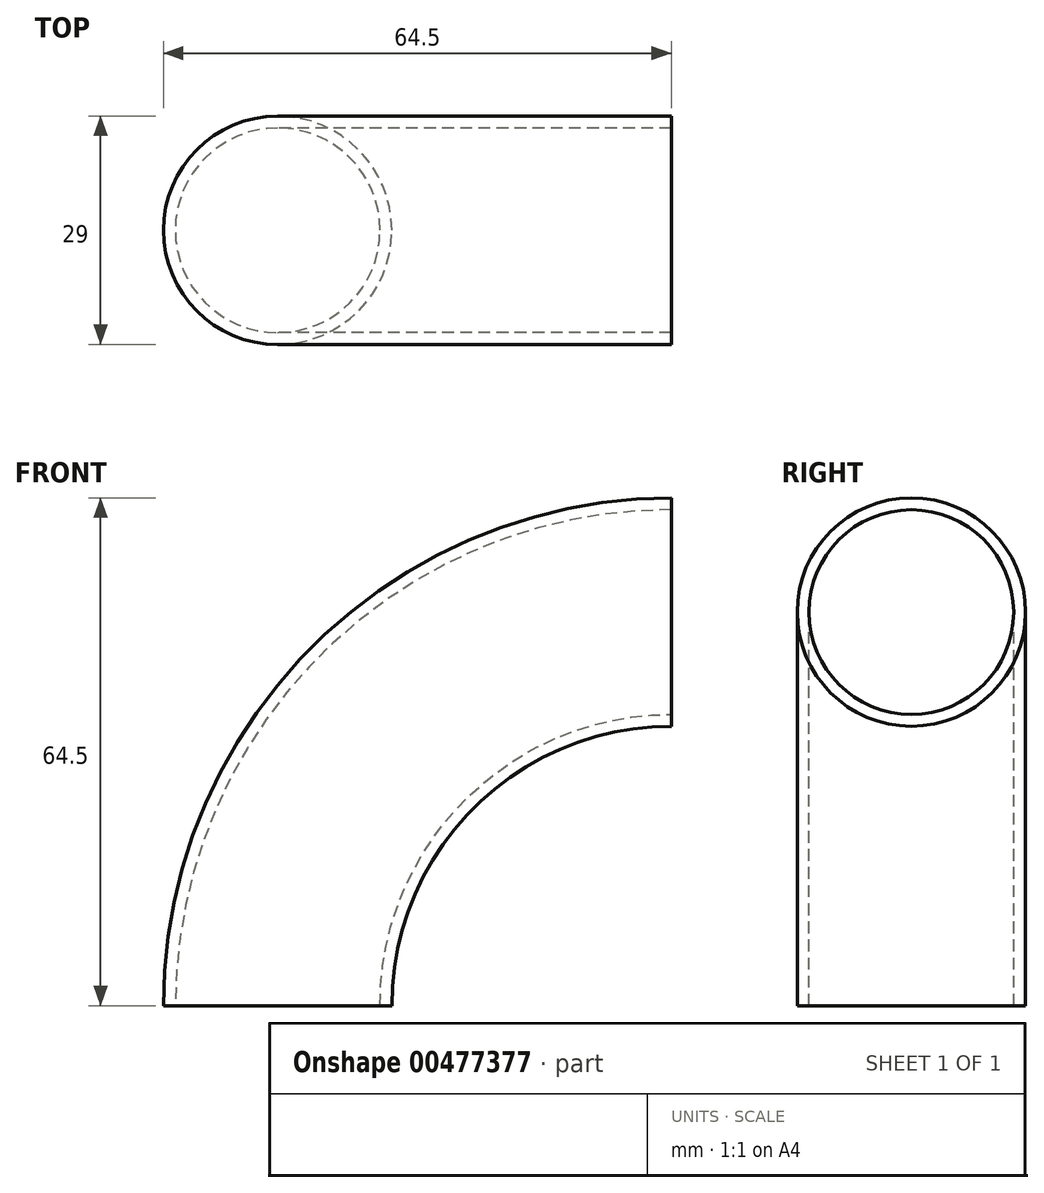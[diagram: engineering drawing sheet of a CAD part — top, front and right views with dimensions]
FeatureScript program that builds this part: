
annotation { "Feature Type Name" : "Feature", "Feature Type Description" : "" }
export const myFeature = defineFeature(function(context is Context, id is Id, definition is map)
    precondition{}
    {
        {
            var Q0;
            Q0=qCreatedBy(makeId("Front.planeOp"),FACE);
            var sketch = newSketch(context, id + "F0", { "sketchPlane" : qUnion([Q0])});
            skArc(sketch, "E0", {"start": v(0, 50) * mm, "mid": v(-35.36, 35.36) * mm, "end": v(-50, 0) * mm});
            skLineSegment(sketch, "E1", {"start": v(0, 0) * mm, "end": v(-50, 0) * mm, "construction": true});
            skLineSegment(sketch, "E2", {"start": v(0, 0) * mm, "end": v(0, 50) * mm, "construction": true});
            skSolve(sketch);
        }
        {
            var Q0;
            Q0=qCreatedBy(makeId("Top.planeOp"),FACE);
            var sketch = newSketch(context, id + "F1", { "sketchPlane" : qUnion([Q0])});
            skCircle(sketch, "E3", {"center": v(-50, 0) * mm, "radius": 13 * mm});
            skCircle(sketch, "E4", {"center": v(-50, 0) * mm, "radius": 14.5 * mm});
            skSolve(sketch);
        }
        {
            var Q0;
            Q0=makeQuery(id+"F1.imprint","IMPRINT",FACE,{"disambiguationData":[TD([[makeQuery(id+"F1.imprint","IMPRINT",EDGE,{"derivedFrom":sQuery(id+"F1.wireOp",EDGE,"E3")}),-1.0]])]});
            var Q1;
            Q1=qConstructionFilter(qBodyType(qCreatedBy(id+"F1",EDGE),BodyType.WIRE),ConstructionObject.NO);
            var Q2;
            Q2=sQuery(id+"F0.wireOp",EDGE,"E0");
            sweep(context, id + "F2", {"profiles" : qUnion([Q0]), "surfaceProfiles" : qUnion([Q1]), "path" : qUnion([Q2])});
        }
    });
